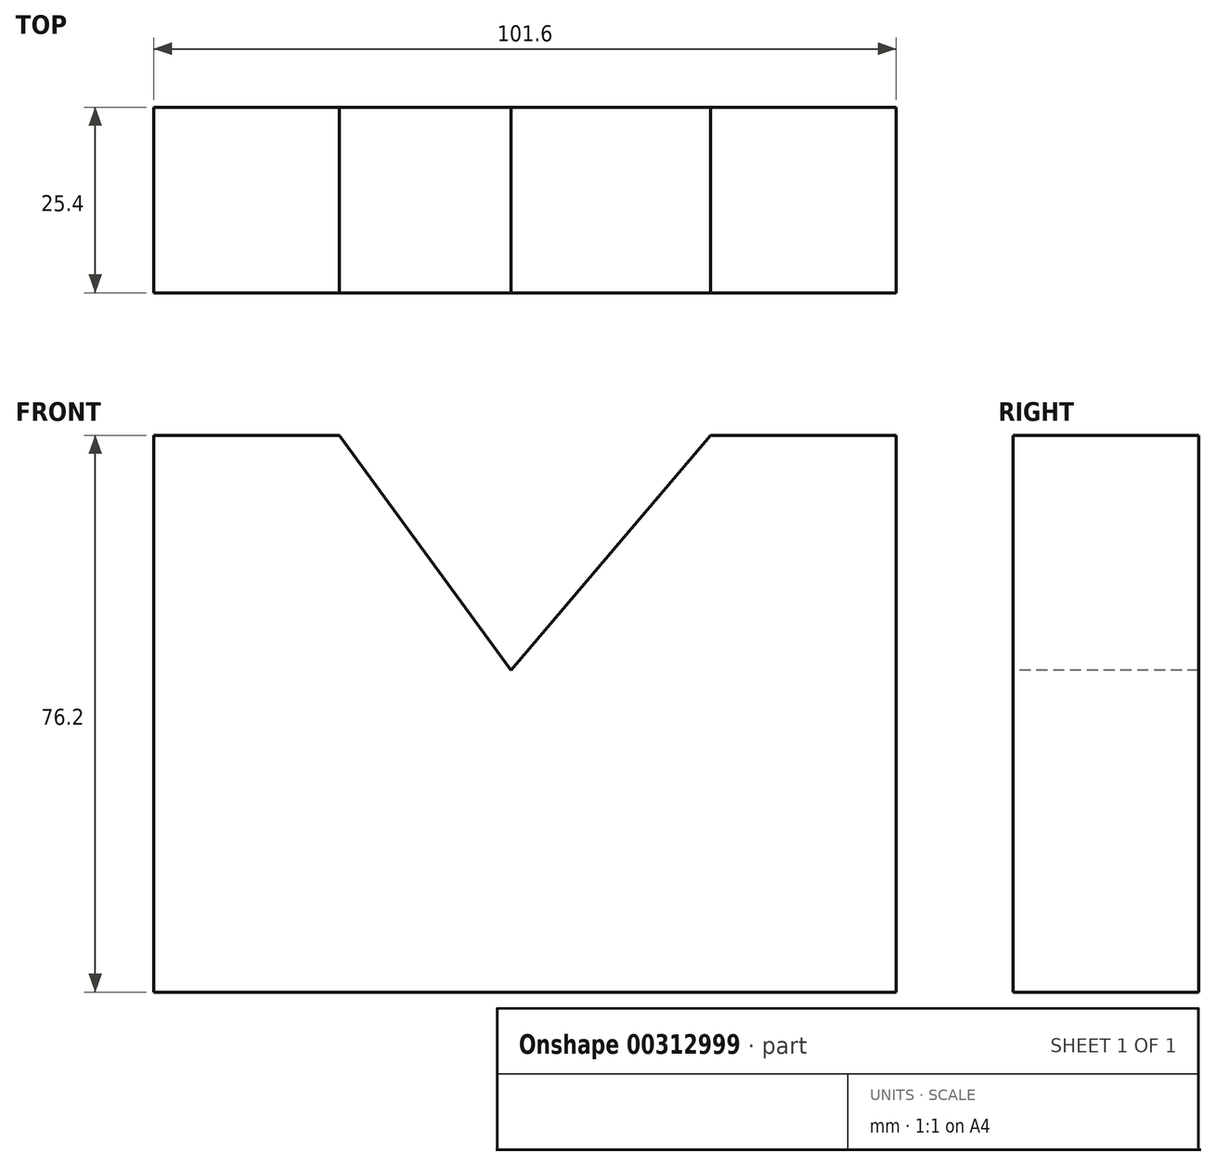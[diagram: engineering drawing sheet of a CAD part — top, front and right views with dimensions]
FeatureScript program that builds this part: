
annotation { "Feature Type Name" : "Feature", "Feature Type Description" : "" }
export const myFeature = defineFeature(function(context is Context, id is Id, definition is map)
    precondition{}
    {
        {
            var Q0;
            Q0=qCreatedBy(makeId("Front.planeOp"),FACE);
            var sketch = newSketch(context, id + "F0", { "sketchPlane" : qUnion([Q0])});
            skLineSegment(sketch, "E0", {"start": v(-41.74, -55.5) * mm, "end": v(59.86, -55.5) * mm});
            skLineSegment(sketch, "E1", {"start": v(59.86, -55.5) * mm, "end": v(59.86, 20.7) * mm});
            skLineSegment(sketch, "E2", {"start": v(59.86, 20.7) * mm, "end": v(34.46, 20.7) * mm});
            skLineSegment(sketch, "E3", {"start": v(34.46, 20.7) * mm, "end": v(7.17, -11.45) * mm});
            skLineSegment(sketch, "E4", {"start": v(7.17, -11.45) * mm, "end": v(-16.34, 20.7) * mm});
            skLineSegment(sketch, "E5", {"start": v(-16.34, 20.7) * mm, "end": v(-41.74, 20.7) * mm});
            skLineSegment(sketch, "E6", {"start": v(-41.74, 20.7) * mm, "end": v(-41.74, -55.5) * mm});
            skSolve(sketch);
        }
        {
            var Q0;
            Q0=makeQuery(id+"F0.imprint","IMPRINT",FACE,{"disambiguationData":[TD([[makeQuery(id+"F0.imprint","IMPRINT",EDGE,{"derivedFrom":sQuery(id+"F0.wireOp",EDGE,"E0")}),1.0]])]});
            extrude(context, id + "F1", {"entities" : qUnion([Q0]), "oppositeDirection" : true, "depth" : 25.4 * mm});
        }
    });
